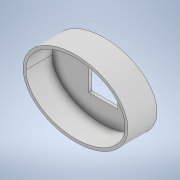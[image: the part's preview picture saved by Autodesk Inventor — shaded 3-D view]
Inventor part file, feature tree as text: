
AUTODESK INVENTOR PART (.ipt)
format: ipt  version: 2020 (Build 240168000, 168)  size: 130,048 bytes
history: native  units: mm
features: extrude x2, sketch x2, shell x1
ambient origin geometry x8: Origin, YZ Plane, XZ Plane, XY Plane, X Axis, Y Axis, Z Axis, Center Point
bodies: Solid1 (feature_tree)
feature tree (5):
  extrude  "Extrusion1"  Depth=50.0mm
  shell  "Shell1"  Thickness=50.0mm
  extrude  "Extrusion2"  Depth=50.0mm
  sketch  "Sketch1"  dims[d2=65.0mm d3=90.0mm d4=50.0mm d5=0.0mm]
  sketch  "Sketch2"  dims[d6=5.0mm d7=50.0mm d8=50.0mm d9=10.0mm d10=0.0mm]
